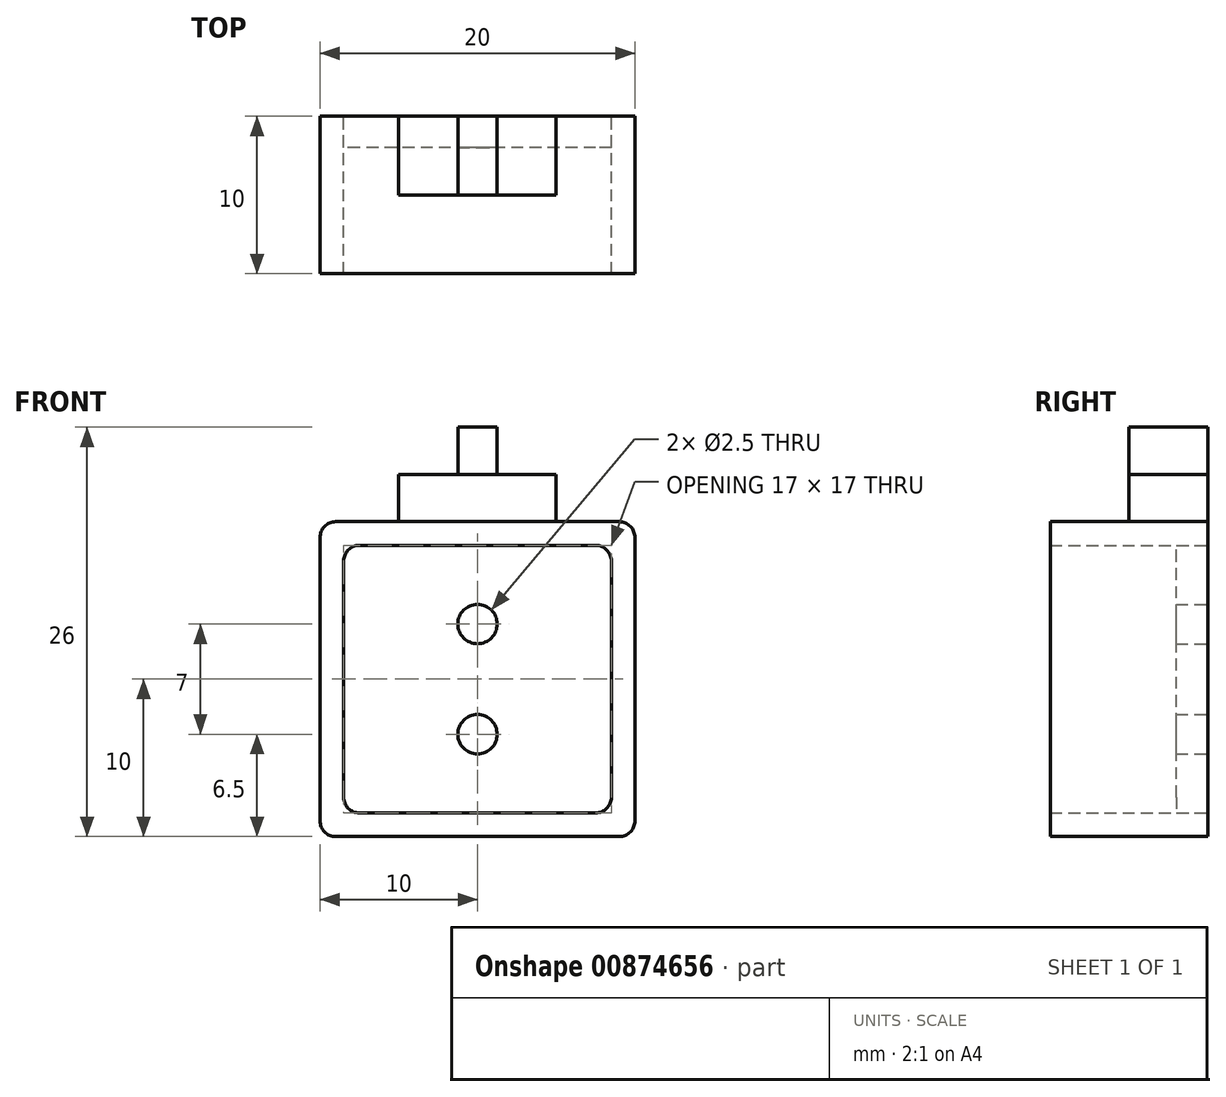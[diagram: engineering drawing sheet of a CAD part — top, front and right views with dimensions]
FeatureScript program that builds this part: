
annotation { "Feature Type Name" : "Feature", "Feature Type Description" : "" }
export const myFeature = defineFeature(function(context is Context, id is Id, definition is map)
    precondition{}
    {
        {
            var Q0;
            Q0=qCreatedBy(makeId("Front.planeOp"),FACE);
            var sketch = newSketch(context, id + "F0", { "sketchPlane" : qUnion([Q0])});
            skCircle(sketch, "E0", {"center": v(0, -3.5) * mm, "radius": 1.25 * mm});
            skCircle(sketch, "E1", {"center": v(0, 3.5) * mm, "radius": 1.25 * mm});
            skPoint(sketch, "E2.middle", {"position": v(0, 12.44) * mm});
            skLineSegment(sketch, "E3.bottom", {"start": v(1.25, 10) * mm, "end": v(-1.25, 10) * mm});
            skLineSegment(sketch, "E3.top", {"start": v(1.25, 16) * mm, "end": v(-1.25, 16) * mm});
            skLineSegment(sketch, "E3.left", {"start": v(1.25, 10) * mm, "end": v(1.25, 16) * mm});
            skLineSegment(sketch, "E3.right", {"start": v(-1.25, 10) * mm, "end": v(-1.25, 16) * mm});
            skPoint(sketch, "E3.middle", {"position": v(0, 13) * mm});
            skLineSegment(sketch, "E4.bottom", {"start": v(9, -10) * mm, "end": v(-9, -10) * mm});
            skLineSegment(sketch, "E4.top", {"start": v(9, 10) * mm, "end": v(-9, 10) * mm});
            skLineSegment(sketch, "E4.left", {"start": v(10, -9) * mm, "end": v(10, 9) * mm});
            skLineSegment(sketch, "E4.right", {"start": v(-10, -9) * mm, "end": v(-10, 9) * mm});
            skPoint(sketch, "E4.middle", {"position": v(0, 0) * mm});
            skPoint(sketch, "E5.visualSharp", {"position": v(-10, 10) * mm});
            skArc(sketch, "E5.filletArc", {"start": v(-9, 10) * mm, "mid": v(-9.7, 9.7) * mm, "end": v(-10, 9) * mm});
            skPoint(sketch, "E6.visualSharp", {"position": v(10, 10) * mm});
            skArc(sketch, "E6.filletArc", {"start": v(10, 9) * mm, "mid": v(9.7, 9.7) * mm, "end": v(9, 10) * mm});
            skPoint(sketch, "E7.visualSharp", {"position": v(-10, -10) * mm});
            skArc(sketch, "E7.filletArc", {"start": v(-10, -9) * mm, "mid": v(-9.7, -9.7) * mm, "end": v(-9, -10) * mm});
            skPoint(sketch, "E8.visualSharp", {"position": v(10, -10) * mm});
            skArc(sketch, "E8.filletArc", {"start": v(9, -10) * mm, "mid": v(9.7, -9.7) * mm, "end": v(10, -9) * mm});
            skLineSegment(sketch, "E9.bottom", {"start": v(7.5, -8.5) * mm, "end": v(-7.5, -8.5) * mm});
            skLineSegment(sketch, "E9.top", {"start": v(7.5, 8.5) * mm, "end": v(-7.5, 8.5) * mm});
            skLineSegment(sketch, "E9.left", {"start": v(8.5, -7.5) * mm, "end": v(8.5, 7.5) * mm});
            skLineSegment(sketch, "E9.right", {"start": v(-8.5, -7.5) * mm, "end": v(-8.5, 7.5) * mm});
            skPoint(sketch, "E10.visualSharp", {"position": v(-8.5, 8.5) * mm});
            skArc(sketch, "E10.filletArc", {"start": v(-7.5, 8.5) * mm, "mid": v(-8.2, 8.2) * mm, "end": v(-8.5, 7.5) * mm});
            skPoint(sketch, "E11.visualSharp", {"position": v(8.5, 8.5) * mm});
            skArc(sketch, "E11.filletArc", {"start": v(8.5, 7.5) * mm, "mid": v(8.2, 8.2) * mm, "end": v(7.5, 8.5) * mm});
            skPoint(sketch, "E12.visualSharp", {"position": v(8.5, -8.5) * mm});
            skArc(sketch, "E12.filletArc", {"start": v(7.5, -8.5) * mm, "mid": v(8.2, -8.2) * mm, "end": v(8.5, -7.5) * mm});
            skPoint(sketch, "E13.visualSharp", {"position": v(-8.5, -8.5) * mm});
            skArc(sketch, "E13.filletArc", {"start": v(-8.5, -7.5) * mm, "mid": v(-8.2, -8.2) * mm, "end": v(-7.5, -8.5) * mm});
            skLineSegment(sketch, "E14.bottom", {"start": v(5, 10) * mm, "end": v(-5, 10) * mm});
            skLineSegment(sketch, "E14.top", {"start": v(5, 13) * mm, "end": v(-5, 13) * mm});
            skLineSegment(sketch, "E14.left", {"start": v(5, 10) * mm, "end": v(5, 13) * mm});
            skLineSegment(sketch, "E14.right", {"start": v(-5, 10) * mm, "end": v(-5, 13) * mm});
            skPoint(sketch, "E14.middle", {"position": v(0, 11.5) * mm});
            skSolve(sketch);
        }
        {
            var Q0;
            {var subQ0=sQuery(id+"F0.wireOp",EDGE,"E3.top");Q0=makeQuery(id+"F0.imprint","IMPRINT",FACE,{"disambiguationData":[TD([[makeQuery(id+"F0.imprint","IMPRINT",EDGE,{"derivedFrom":subQ0}),1.0]])]});}
            extrude(context, id + "F1", {"entities" : qUnion([Q0]), "depth" : 5 * mm, "offsetDistance" : 25 * mm});
        }
        {
            var Q0;
            Q0=makeQuery(id+"F0.imprint","IMPRINT",FACE,{"disambiguationData":[TD([[makeQuery(id+"F0.imprint","IMPRINT",EDGE,{"derivedFrom":sQuery(id+"F0.wireOp",EDGE,"E0")}),-1.0]])]});
            extrude(context, id + "F2", {"entities" : qUnion([Q0]), "depth" : 2 * mm, "offsetDistance" : 25 * mm});
        }
        {
            var Q0;
            {var subQ3=sQuery(id+"F0.wireOp",EDGE,"E3.bottom");Q0=makeQuery(id+"F0.imprint","IMPRINT",FACE,{"disambiguationData":[TD([[makeQuery(id+"F0.imprint","IMPRINT",EDGE,{"derivedFrom":subQ3}),1.0]])]});}
            extrude(context, id + "F3", {"entities" : qUnion([Q0]), "depth" : 10 * mm, "offsetDistance" : 25 * mm});
        }
        {
            var Q0;
            {var subQ5=sQuery(id+"F0.wireOp",EDGE,"E14.right");Q0=makeQuery(id+"F0.imprint","IMPRINT",FACE,{"disambiguationData":[TD([[makeQuery(id+"F0.imprint","IMPRINT",EDGE,{"derivedFrom":subQ5}),-1.0]])]});}
            var Q1;
            {var subQ0=sQuery(id+"F0.wireOp",EDGE,"E3.bottom");Q1=makeQuery(id+"F0.imprint","IMPRINT",FACE,{"disambiguationData":[TD([[makeQuery(id+"F0.imprint","IMPRINT",EDGE,{"derivedFrom":subQ0}),-1.0]])]});}
            var Q2;
            {var subQ5=sQuery(id+"F0.wireOp",EDGE,"E14.left");Q2=makeQuery(id+"F0.imprint","IMPRINT",FACE,{"disambiguationData":[TD([[makeQuery(id+"F0.imprint","IMPRINT",EDGE,{"derivedFrom":subQ5}),1.0]])]});}
            extrude(context, id + "F4", {"entities" : qUnion([Q0, Q1, Q2]), "depth" : 5 * mm, "offsetDistance" : 25 * mm});
        }
    });
